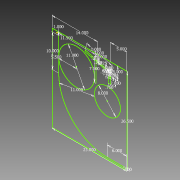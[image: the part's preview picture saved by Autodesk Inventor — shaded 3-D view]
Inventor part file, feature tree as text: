
AUTODESK INVENTOR PART (.ipt)
format: ipt  version: 2012 (Build 160160000, 160)  size: 96,768 bytes
history: native  units: in
note: dims shown in document units (in); Inventor stores cm internally (conversion verified against a paired STEP export)
features: sketch x1
ambient origin geometry x8: Origin, YZ Plane, XZ Plane, XY Plane, X Axis, Y Axis, Z Axis, Center Point
feature tree (1):
  sketch  "Sketch1"  dims[d0=23.0in d1=26.5in d2=8.0in d3=11.0in d4=10.0in d7=11.0in d8=6.0in d9=0.0in d17=5.5in d18=7.0in d19=11.5in d20=1.0in d21=1.0in d25=0.5in d26=8.0in d27=0.25in d28=4.0in d29=2.0in d30=14.0in d31=0.25in d32=0.75in d33=2.0in d34=1.75in d36=0.125in d37=0.25in d38=0.25in d39=0.125in d41=0.125in d42=0.125in d44=0.25in d45=0.25in d46=5.0in d47=4.0in]
